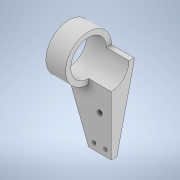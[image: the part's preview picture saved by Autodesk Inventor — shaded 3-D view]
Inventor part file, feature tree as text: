
AUTODESK INVENTOR PART (.ipt)
format: ipt  version: 2021 (Build 250183000, 183)  size: 177,152 bytes
history: native  units: in
note: dims shown in document units (in); Inventor stores cm internally (conversion verified against a paired STEP export)
features: sketch x7, other x3, extrude x1, plane x1
ambient origin geometry x8: Origin, YZ Plane, XZ Plane, XY Plane, X Axis, Y Axis, Z Axis, Center Point
bodies: Solid1 (feature_tree)
feature tree (12):
  other  "motor_tensioner_right.ipt"
  extrude  "Extrusion1"  Depth=0.3937in
  other  "Solid1::motor_tensioner_right.ipt"
  other  "TaggingFeature1"
  sketch  "Sketch1"  dims[d0=0.3937in d1=2.4803in]
  sketch  "Sketch2"  dims[d2=0.3937in d3=0.0in]
  sketch  "Sketch3"
  sketch  "Sketch4"
  sketch  "Sketch5"
  sketch  "Sketch6"
  plane  "Work Plane1"
  sketch  "Sketch7"
